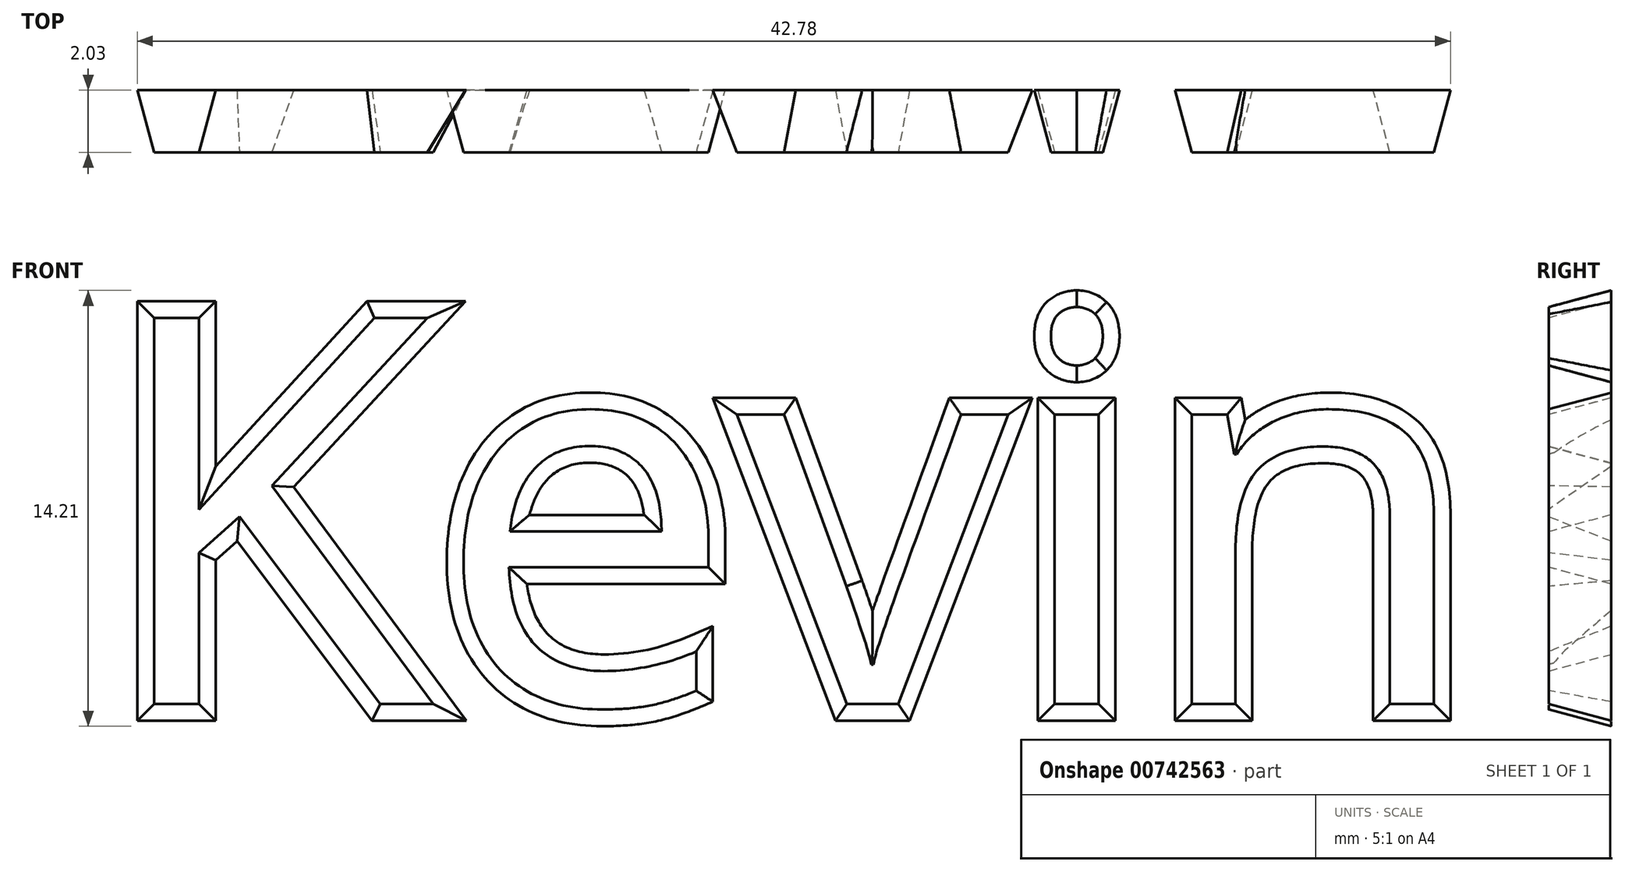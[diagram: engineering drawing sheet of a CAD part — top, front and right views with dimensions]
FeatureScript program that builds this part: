
annotation { "Feature Type Name" : "Feature", "Feature Type Description" : "" }
export const myFeature = defineFeature(function(context is Context, id is Id, definition is map)
    precondition{}
    {
        {
            var Q0;
            Q0=qCreatedBy(makeId("Front.planeOp"),FACE);
            var sketch = newSketch(context, id + "F0", { "sketchPlane" : qUnion([Q0])});
            skLineSegment(sketch, "E0.bottom", {"start": v(-25.4, 15.88) * mm, "end": v(25.4, 15.88) * mm});
            skLineSegment(sketch, "E0.top", {"start": v(-25.4, -15.88) * mm, "end": v(25.4, -15.88) * mm});
            skLineSegment(sketch, "E0.left", {"start": v(-25.4, 15.88) * mm, "end": v(-25.4, -15.88) * mm});
            skLineSegment(sketch, "E0.right", {"start": v(25.4, 15.87) * mm, "end": v(25.4, -15.88) * mm});
            skPoint(sketch, "E0.middle", {"position": v(0, 0) * mm});
            skSolve(sketch);
        }
        {
            var Q0;
            Q0=qCreatedBy(makeId("Front.planeOp"),FACE);
            var sketch = newSketch(context, id + "F1", { "sketchPlane" : qUnion([Q0])});
            skText(sketch, "E1", { "text": "Kevin", "fontName": "OpenSans-Regular.ttf"});
            const initialGuessF1  = {"E1": [-0.02229, -0.00635, 1, 0, 0.0127]};
            skSetInitialGuess(sketch, initialGuessF1);
            skSolve(sketch);
        }
        {
            var Q0;
            Q0=qSketchRegion(id+"F1",true);
            extrude(context, id + "F2", {"entities" : qUnion([Q0]), "oppositeDirection" : true, "depth" : 2.03 * mm, "offsetDistance" : 25.4 * mm, "hasDraft" : true, "draftAngle" : 15 * degree});
        }
    });
